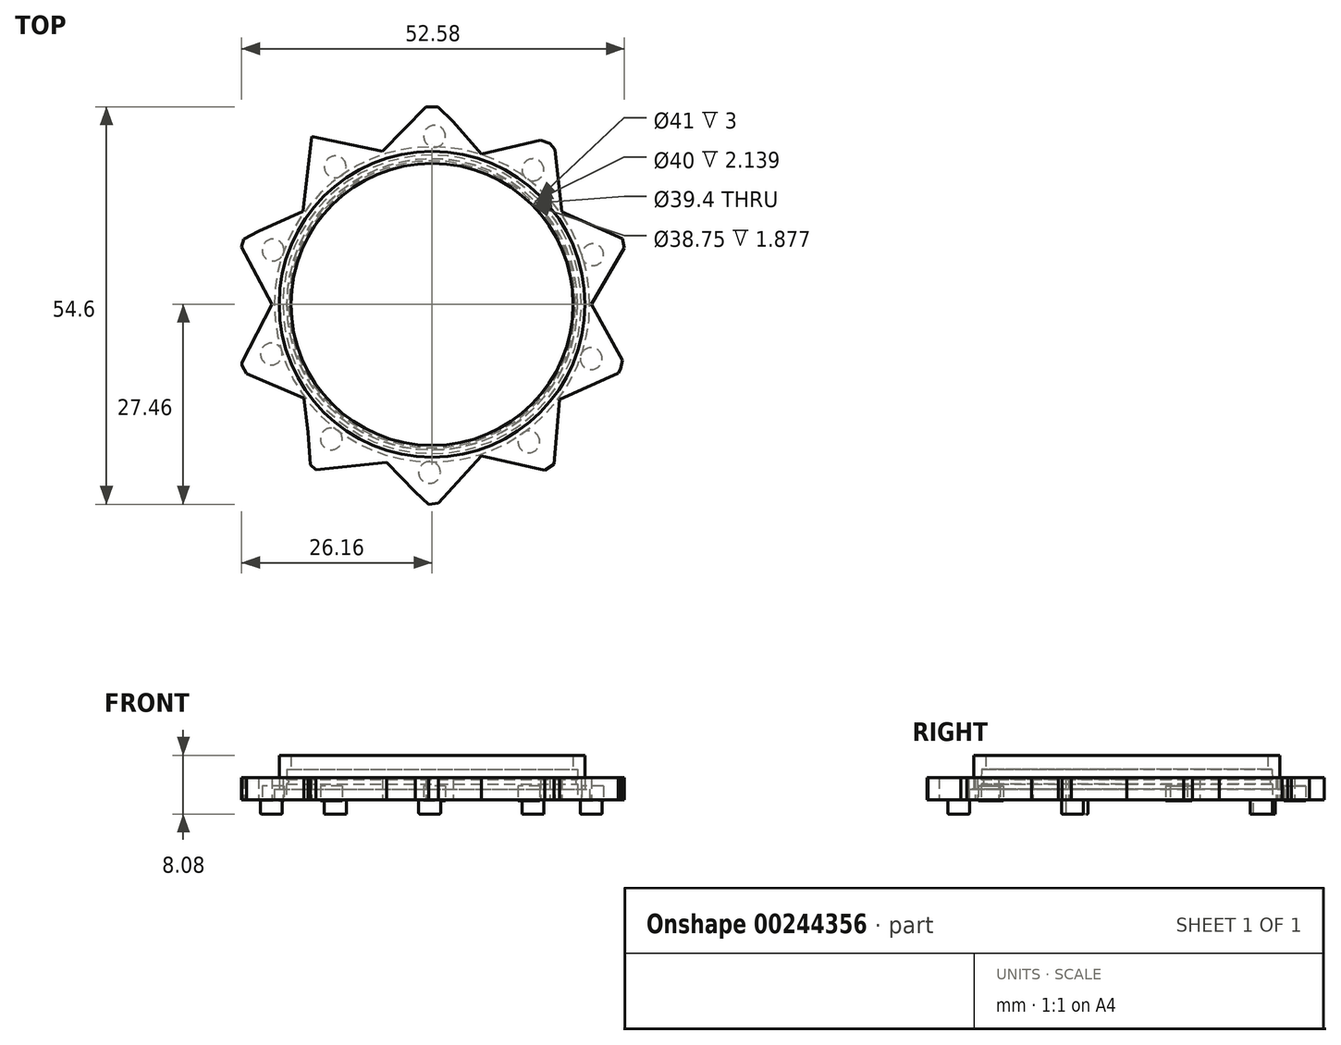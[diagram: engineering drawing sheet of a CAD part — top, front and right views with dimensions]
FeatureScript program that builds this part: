
annotation { "Feature Type Name" : "Feature", "Feature Type Description" : "" }
export const myFeature = defineFeature(function(context is Context, id is Id, definition is map)
    precondition{}
    {
        {
            var Q0;
            Q0=qCreatedBy(makeId("Front.planeOp"),FACE);
            var sketch = newSketch(context, id + "F0", { "sketchPlane" : qUnion([Q0])});
            skLineSegment(sketch, "E0", {"start": v(-21, 1.34) * mm, "end": v(-21, -1.42) * mm});
            skLineSegment(sketch, "E1", {"start": v(-21, -1.42) * mm, "end": v(-10.3, -1.42) * mm});
            skLineSegment(sketch, "E2.bottom", {"start": v(-19.79, 1.26) * mm, "end": v(-20, 1.35) * mm});
            skLineSegment(sketch, "E2.top", {"start": v(-19.38, 2.75) * mm, "end": v(-19.97, 2.75) * mm});
            skLineSegment(sketch, "E2.right", {"start": v(-20, 1.35) * mm, "end": v(-19.97, 2.75) * mm});
            skLineSegment(sketch, "E3.trimOffspring", {"start": v(-19.7, 1.12) * mm, "end": v(-19.7, 0.97) * mm});
            skLineSegment(sketch, "E4", {"start": v(0, -11.48) * mm, "end": v(0, 19.75) * mm, "construction": true});
            skLineSegment(sketch, "E5", {"start": v(-20, -1.42) * mm, "end": v(-20, 0.72) * mm});
            skLineSegment(sketch, "E6", {"start": v(-20, 0.72) * mm, "end": v(-19.78, 0.84) * mm});
            skArc(sketch, "E7.0", {"start": v(-19.73, 1.23) * mm, "mid": v(11.67, -18.8) * mm, "end": v(0, 16.57) * mm, "construction": true});
            skLineSegment(sketch, "E8", {"start": v(-21.17, 0) * mm, "end": v(-21, 0) * mm});
            skLineSegment(sketch, "E9", {"start": v(-21.26, -1.42) * mm, "end": v(-21, -1.42) * mm});
            skPoint(sketch, "E10.visualSharp", {"position": v(-19.7, 1.22) * mm});
            skArc(sketch, "E10.filletArc", {"start": v(-19.7, 1.12) * mm, "mid": v(-19.72, 1.2) * mm, "end": v(-19.79, 1.26) * mm});
            skPoint(sketch, "E11.visualSharp", {"position": v(-19.7, 0.88) * mm});
            skArc(sketch, "E11.filletArc", {"start": v(-19.78, 0.84) * mm, "mid": v(-19.72, 0.9) * mm, "end": v(-19.7, 0.97) * mm});
            skLineSegment(sketch, "E12", {"start": v(-19.38, 2.75) * mm, "end": v(-19.38, 4.63) * mm});
            skLineSegment(sketch, "E13", {"start": v(-19.38, 4.63) * mm, "end": v(-21, 4.66) * mm});
            skLineSegment(sketch, "E14", {"start": v(-21, 4.66) * mm, "end": v(-21, 1.34) * mm});
            skLineSegment(sketch, "E15", {"start": v(-21, -1.42) * mm, "end": v(-21.65, -1.42) * mm});
            skLineSegment(sketch, "E16", {"start": v(-21.65, -1.42) * mm, "end": v(-21.65, 0) * mm});
            skLineSegment(sketch, "E17", {"start": v(-21.65, 0) * mm, "end": v(-21, 0) * mm});
            skLineSegment(sketch, "E18", {"start": v(-19.38, 4.63) * mm, "end": v(-18.61, 4.63) * mm});
            skLineSegment(sketch, "E19", {"start": v(0, 19.75) * mm, "end": v(0, 16.57) * mm});
            skSolve(sketch);
        }
        {
            var Q0;
            Q0=qSketchRegion(id+"F0",true);
            var Q1;
            Q1=sQuery(id+"F0.wireOp",EDGE,"E4");
            revolve(context, id + "F1", {"entities" : qUnion([Q0]), "axis" : qUnion([Q1]), "revolveType" : RevolveType.FULL});
        }
        {
            var Q0;
            Q0=qCreatedBy(makeId("Top.planeOp"),FACE);
            cPlane(context, id + "F2", {"entities" : qUnion([Q0]), "cplaneType" : CPlaneType.OFFSET, "offset" : 1.56 * mm, "oppositeDirection" : true, "width" : 150 * mm, "height" : 150 * mm});
        }
        {
            var Q0;
            Q0=makeQuery(id+"F1.opRevolve","SWEPT_FACE",FACE,{"disambiguationData":[OSD([sQuery(id+"F0.wireOp",EDGE,"E1"),sQuery(id+"F0.wireOp",EDGE,"E15")])]});
            var sketch = newSketch(context, id + "F3", { "sketchPlane" : qUnion([Q0])});
            skLineSegment(sketch, "E20", {"start": v(-17.58, 12.88) * mm, "end": v(-25.51, 9.49) * mm});
            skLineSegment(sketch, "E21", {"start": v(-25.51, 9.49) * mm, "end": v(-26.15, 8.38) * mm});
            skLineSegment(sketch, "E22", {"start": v(-26.15, 8.38) * mm, "end": v(-26.15, 8) * mm});
            skLineSegment(sketch, "E23", {"start": v(-26.15, 8) * mm, "end": v(-21.97, 0) * mm});
            skLineSegment(sketch, "E24", {"start": v(-21.97, 0) * mm, "end": v(-26.16, -7.9) * mm});
            skLineSegment(sketch, "E25", {"start": v(-26.16, -7.9) * mm, "end": v(-25.9, -8.95) * mm});
            skLineSegment(sketch, "E26", {"start": v(-25.9, -8.95) * mm, "end": v(-23.85, -10.05) * mm});
            skLineSegment(sketch, "E27", {"start": v(-23.85, -10.05) * mm, "end": v(-17.75, -12.76) * mm});
            skLineSegment(sketch, "E28", {"start": v(-17.75, -12.76) * mm, "end": v(-16.55, -23.04) * mm});
            skLineSegment(sketch, "E29", {"start": v(-16.55, -23.04) * mm, "end": v(-6.8, -21) * mm});
            skLineSegment(sketch, "E30", {"start": v(-6.8, -21) * mm, "end": v(-0.87, -27.14) * mm});
            skLineSegment(sketch, "E31", {"start": v(-0.87, -27.14) * mm, "end": v(0.82, -27.14) * mm});
            skLineSegment(sketch, "E32", {"start": v(0.82, -27.14) * mm, "end": v(2.9, -25.08) * mm});
            skLineSegment(sketch, "E33", {"start": v(2.9, -25.08) * mm, "end": v(6.76, -20.67) * mm});
            skLineSegment(sketch, "E34", {"start": v(6.76, -20.67) * mm, "end": v(14.9, -22.58) * mm});
            skLineSegment(sketch, "E35", {"start": v(14.9, -22.58) * mm, "end": v(16.15, -22.08) * mm});
            skLineSegment(sketch, "E36", {"start": v(16.15, -22.08) * mm, "end": v(16.86, -21.3) * mm});
            skLineSegment(sketch, "E37", {"start": v(16.86, -21.3) * mm, "end": v(17.8, -12.7) * mm});
            skLineSegment(sketch, "E38", {"start": v(17.8, -12.7) * mm, "end": v(26.11, -9.03) * mm});
            skLineSegment(sketch, "E39", {"start": v(26.11, -9.03) * mm, "end": v(26.42, -7.78) * mm});
            skLineSegment(sketch, "E40", {"start": v(26.42, -7.78) * mm, "end": v(21.9, 0) * mm});
            skLineSegment(sketch, "E41", {"start": v(21.9, 0) * mm, "end": v(26.11, 7.65) * mm});
            skLineSegment(sketch, "E42", {"start": v(26.11, 7.65) * mm, "end": v(25.91, 8.88) * mm});
            skLineSegment(sketch, "E43", {"start": v(25.91, 8.88) * mm, "end": v(25.59, 9.42) * mm});
            skLineSegment(sketch, "E44", {"start": v(25.59, 9.42) * mm, "end": v(17.53, 13.07) * mm});
            skLineSegment(sketch, "E45", {"start": v(17.53, 13.07) * mm, "end": v(16.71, 21.96) * mm});
            skLineSegment(sketch, "E46", {"start": v(16.71, 21.96) * mm, "end": v(15.48, 22.77) * mm});
            skLineSegment(sketch, "E47", {"start": v(15.48, 22.77) * mm, "end": v(6.78, 20.84) * mm});
            skLineSegment(sketch, "E48", {"start": v(6.78, 20.84) * mm, "end": v(0.86, 27.31) * mm});
            skLineSegment(sketch, "E49", {"start": v(0.86, 27.31) * mm, "end": v(-0.45, 27.46) * mm});
            skLineSegment(sketch, "E50", {"start": v(-0.45, 27.46) * mm, "end": v(-2.3, 25.78) * mm});
            skLineSegment(sketch, "E51", {"start": v(-2.3, 25.78) * mm, "end": v(-6.27, 21.7) * mm});
            skLineSegment(sketch, "E52", {"start": v(-6.27, 21.7) * mm, "end": v(-15.93, 22.76) * mm});
            skLineSegment(sketch, "E53", {"start": v(-15.93, 22.76) * mm, "end": v(-16.7, 22) * mm});
            skLineSegment(sketch, "E54", {"start": v(-16.7, 22) * mm, "end": v(-17.04, 17.59) * mm});
            skLineSegment(sketch, "E55", {"start": v(-17.04, 17.59) * mm, "end": v(-17.58, 12.88) * mm});
            skCircle(sketch, "E56", {"center": v(0, 0) * mm, "radius": 20.5 * mm});
            skSolve(sketch);
        }
        {
            var Q0;
            Q0 = qSketchRegion(id + "F3", true);
            extrude(context, id + "F4", {"entities" : qUnion([Q0]), "oppositeDirection" : true, "depth" : 3 * mm});
        }
        {
            var Q0;
            Q0=makeQuery(id+"F4.opExtrude","CAP_FACE",FACE,{"disambiguationData":[OSD([sQuery(id+"F3.wireOp",EDGE,"E20"),sQuery(id+"F3.wireOp",EDGE,"E21"),sQuery(id+"F3.wireOp",EDGE,"E22"),sQuery(id+"F3.wireOp",EDGE,"E23"),sQuery(id+"F3.wireOp",EDGE,"E24"),sQuery(id+"F3.wireOp",EDGE,"E25"),sQuery(id+"F3.wireOp",EDGE,"E26"),sQuery(id+"F3.wireOp",EDGE,"E27"),sQuery(id+"F3.wireOp",EDGE,"E28"),sQuery(id+"F3.wireOp",EDGE,"E29"),sQuery(id+"F3.wireOp",EDGE,"E30"),sQuery(id+"F3.wireOp",EDGE,"E31"),sQuery(id+"F3.wireOp",EDGE,"E32"),sQuery(id+"F3.wireOp",EDGE,"E33"),sQuery(id+"F3.wireOp",EDGE,"E34"),sQuery(id+"F3.wireOp",EDGE,"E35"),sQuery(id+"F3.wireOp",EDGE,"E36"),sQuery(id+"F3.wireOp",EDGE,"E37"),sQuery(id+"F3.wireOp",EDGE,"E38"),sQuery(id+"F3.wireOp",EDGE,"E39"),sQuery(id+"F3.wireOp",EDGE,"E40"),sQuery(id+"F3.wireOp",EDGE,"E41"),sQuery(id+"F3.wireOp",EDGE,"E42"),sQuery(id+"F3.wireOp",EDGE,"E43"),sQuery(id+"F3.wireOp",EDGE,"E44"),sQuery(id+"F3.wireOp",EDGE,"E45"),sQuery(id+"F3.wireOp",EDGE,"E46"),sQuery(id+"F3.wireOp",EDGE,"E47"),sQuery(id+"F3.wireOp",EDGE,"E48"),sQuery(id+"F3.wireOp",EDGE,"E49"),sQuery(id+"F3.wireOp",EDGE,"E50"),sQuery(id+"F3.wireOp",EDGE,"E51"),sQuery(id+"F3.wireOp",EDGE,"E52"),sQuery(id+"F3.wireOp",EDGE,"E53"),sQuery(id+"F3.wireOp",EDGE,"E54"),sQuery(id+"F3.wireOp",EDGE,"E55"),sQuery(id+"F3.wireOp",EDGE,"E56")])],"isStart":true});
            var sketch = newSketch(context, id + "F5", { "sketchPlane" : qUnion([Q0])});
            skCircle(sketch, "E57", {"center": v(21.86, 7.46) * mm, "radius": 1.5 * mm});
            skCircle(sketch, "E58.1.0", {"center": v(13.3, 18.88) * mm, "radius": 1.5 * mm, "construction": true});
            skCircle(sketch, "E58.2.0", {"center": v(-0.34, 23.1) * mm, "radius": 1.5 * mm});
            skCircle(sketch, "E58.3.0", {"center": v(-13.85, 18.48) * mm, "radius": 1.5 * mm, "construction": true});
            skCircle(sketch, "E58.4.0", {"center": v(-22.07, 6.81) * mm, "radius": 1.5 * mm});
            skPoint(sketch, "E58.center", {"position": v(0, 0) * mm});
            skCircle(sketch, "E59.1.5.0", {"center": v(-21.86, -7.46) * mm, "radius": 1.5 * mm, "construction": true});
            skCircle(sketch, "E59.1.6.0", {"center": v(-13.3, -18.88) * mm, "radius": 1.5 * mm});
            skCircle(sketch, "E59.1.7.0", {"center": v(0.34, -23.1) * mm, "radius": 1.5 * mm, "construction": true});
            skCircle(sketch, "E59.1.8.0", {"center": v(13.85, -18.48) * mm, "radius": 1.5 * mm});
            skCircle(sketch, "E59.1.9.0", {"center": v(22.07, -6.81) * mm, "radius": 1.5 * mm, "construction": true});
            skSolve(sketch);
        }
        {
            var Q0;
            Q0 = qSketchRegion(id + "F5", true);
            extrude(context, id + "F6", {"entities" : qUnion([Q0]), "depth" : 2 * mm});
        }
        {
            var Q0;
            Q0=makeQuery(id+"F6.opExtrude","CAP_EDGE",EDGE,{"disambiguationData":[OSD([sQuery(id+"F5.wireOp",EDGE,"E58.1.0")])],"isStart":false});
            var Q1;
            Q1=makeQuery(id+"F6.opExtrude","CAP_EDGE",EDGE,{"disambiguationData":[OSD([sQuery(id+"F5.wireOp",EDGE,"E57")])],"isStart":false});
            var Q2;
            Q2=makeQuery(id+"F6.opExtrude","CAP_EDGE",EDGE,{"disambiguationData":[OSD([sQuery(id+"F5.wireOp",EDGE,"E58.4.0")])],"isStart":false});
            var Q3;
            Q3=makeQuery(id+"F6.opExtrude","CAP_EDGE",EDGE,{"disambiguationData":[OSD([sQuery(id+"F5.wireOp",EDGE,"E58.3.0")])],"isStart":false});
            var Q4;
            Q4=makeQuery(id+"F6.opExtrude","CAP_EDGE",EDGE,{"disambiguationData":[OSD([sQuery(id+"F5.wireOp",EDGE,"E58.2.0")])],"isStart":false});
            fillet(context, id + "F7", {"entities" : qUnion([Q0, Q1, Q2, Q3, Q4]), "radius" : .2 * mm, "tangentPropagation" : true, "allowEdgeOverflow" : false});
        }
        {
            var Q0;
            Q0=qCreatedBy(id+"F2.planeOp",FACE);
            var sketch = newSketch(context, id + "F8", { "sketchPlane" : qUnion([Q0])});
            skCircle(sketch, "E60.0", {"center": v(13.3, -18.88) * mm, "radius": 1.5 * mm});
            skCircle(sketch, "E61.1.0", {"center": v(21.86, -7.46) * mm, "radius": 1.5 * mm, "construction": true});
            skCircle(sketch, "E61.2.0", {"center": v(22.07, 6.81) * mm, "radius": 1.5 * mm});
            skCircle(sketch, "E61.3.0", {"center": v(13.85, 18.48) * mm, "radius": 1.5 * mm, "construction": true});
            skCircle(sketch, "E61.4.0", {"center": v(0.34, 23.1) * mm, "radius": 1.5 * mm});
            skCircle(sketch, "E61.5.0", {"center": v(-13.3, 18.88) * mm, "radius": 1.5 * mm, "construction": true});
            skCircle(sketch, "E61.6.0", {"center": v(-21.86, 7.46) * mm, "radius": 1.5 * mm});
            skCircle(sketch, "E61.7.0", {"center": v(-22.07, -6.81) * mm, "radius": 1.5 * mm, "construction": true});
            skCircle(sketch, "E61.8.0", {"center": v(-13.85, -18.48) * mm, "radius": 1.5 * mm});
            skCircle(sketch, "E61.9.0", {"center": v(-0.34, -23.1) * mm, "radius": 1.5 * mm, "construction": true});
            skPoint(sketch, "E61.center", {"position": v(0, 0) * mm});
            skSolve(sketch);
        }
        {
            var Q0;
            Q0 = qSketchRegion(id + "F8", true);
            extrude(context, id + "F9", {"entities" : qUnion([Q0]), "depth" : 2 * mm});
        }
    });
